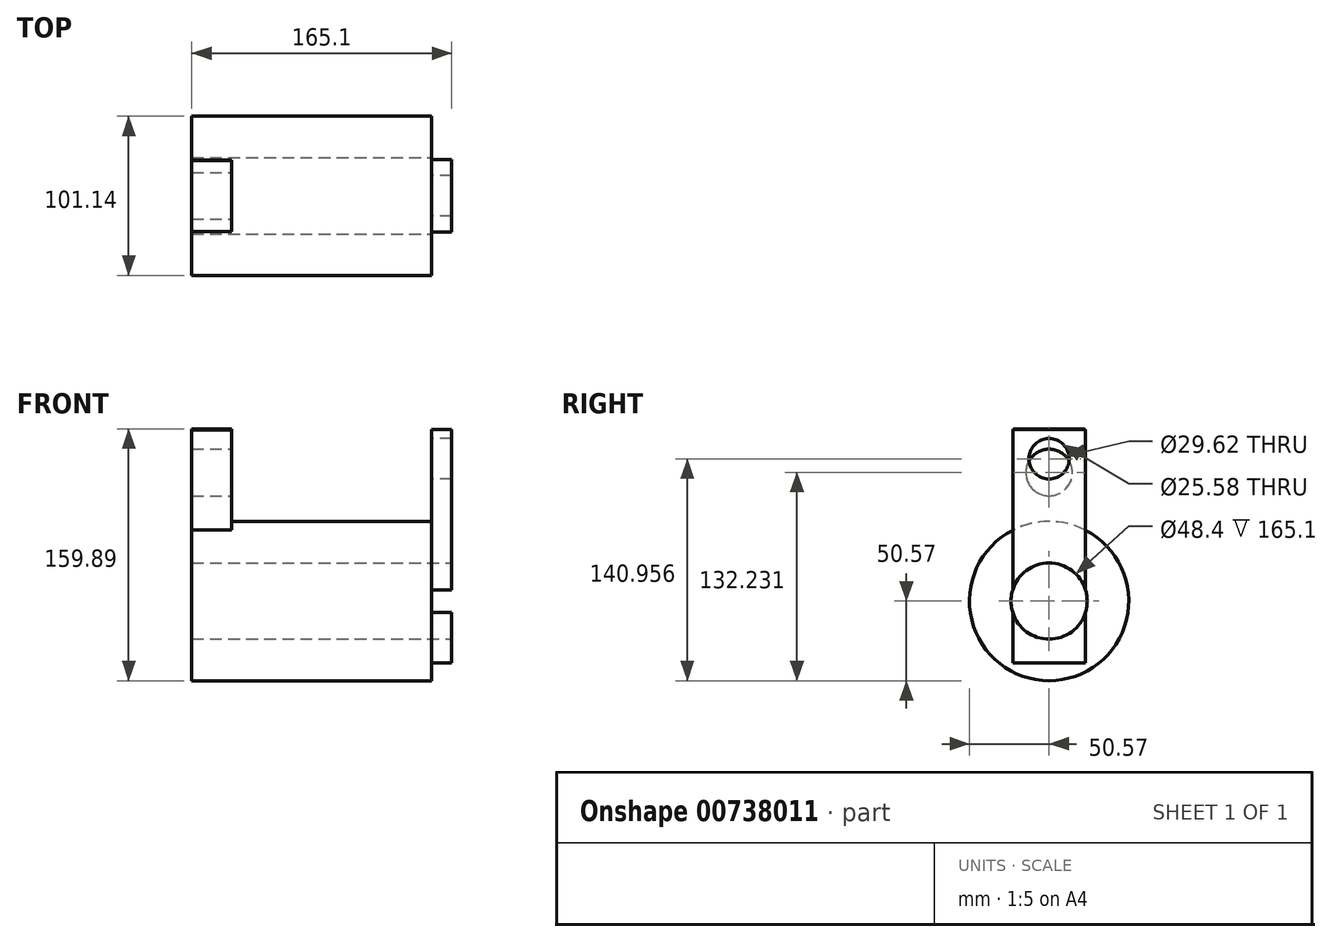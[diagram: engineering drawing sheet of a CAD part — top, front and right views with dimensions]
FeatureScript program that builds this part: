
annotation { "Feature Type Name" : "Feature", "Feature Type Description" : "" }
export const myFeature = defineFeature(function(context is Context, id is Id, definition is map)
    precondition{}
    {
        {
            var Q0;
            Q0=qCreatedBy(makeId("Right.planeOp"),FACE);
            var sketch = newSketch(context, id + "F0", { "sketchPlane" : qUnion([Q0])});
            skCircle(sketch, "E0", {"center": v(0, 0) * mm, "radius": 50.57 * mm});
            skSolve(sketch);
        }
        {
            var Q0;
            Q0 = qSketchRegion(id + "F0", true);
            extrude(context, id + "F1", {"entities" : qUnion([Q0]), "depth" : 152.4 * mm, "offsetDistance" : 25.4 * mm});
        }
        {
            var Q0;
            Q0=qCreatedBy(makeId("Right.planeOp"),FACE);
            var sketch = newSketch(context, id + "F2", { "sketchPlane" : qUnion([Q0])});
            skLineSegment(sketch, "E1.bottom", {"start": v(22.55, 109.32) * mm, "end": v(-22.55, 109.32) * mm});
            skLineSegment(sketch, "E1.top", {"start": v(22.55, -44.03) * mm, "end": v(-22.55, -44.03) * mm});
            skLineSegment(sketch, "E1.left", {"start": v(22.55, 109.32) * mm, "end": v(22.55, -44.03) * mm});
            skLineSegment(sketch, "E1.right", {"start": v(-22.55, 109.32) * mm, "end": v(-22.55, -44.03) * mm});
            skPoint(sketch, "E1.middle", {"position": v(0, 32.65) * mm});
            skSolve(sketch);
        }
        {
            var Q0;
            Q0 = qSketchRegion(id + "F2", true);
            extrude(context, id + "F3", {"entities" : qUnion([Q0]), "operationType" : NewBodyOperationType.ADD, "depth" : 25.4 * mm, "offsetDistance" : 25.4 * mm});
        }
        {
            var Q0;
            Q0=qCreatedBy(makeId("Right.planeOp"),FACE);
            var sketch = newSketch(context, id + "F4", { "sketchPlane" : qUnion([Q0])});
            skLineSegment(sketch, "E2.bottom", {"start": v(-22.66, 108.8) * mm, "end": v(22.66, 108.8) * mm});
            skLineSegment(sketch, "E2.top", {"start": v(-22.66, -44.85) * mm, "end": v(22.66, -44.85) * mm});
            skLineSegment(sketch, "E2.left", {"start": v(-22.66, 108.8) * mm, "end": v(-22.66, -44.85) * mm});
            skLineSegment(sketch, "E2.right", {"start": v(22.66, 108.8) * mm, "end": v(22.66, -44.85) * mm});
            skPoint(sketch, "E2.middle", {"position": v(0, 31.97) * mm});
            skSolve(sketch);
        }
        {
            var Q0;
            Q0 = qSketchRegion(id + "F4", true);
            extrude(context, id + "F5", {"entities" : qUnion([Q0]), "operationType" : NewBodyOperationType.ADD, "depth" : 25.4 * mm, "offsetDistance" : 25.4 * mm});
        }
        {
            var Q0;
            Q0=makeQuery(id+"F1.opExtrude","CAP_FACE",FACE,{"disambiguationData":[OSD([sQuery(id+"F0.wireOp",EDGE,"E0")])],"isStart":false});
            var sketch = newSketch(context, id + "F6", { "sketchPlane" : qUnion([Q0])});
            skLineSegment(sketch, "E3.bottom", {"start": v(-23.12, 109.08) * mm, "end": v(23.12, 109.08) * mm});
            skLineSegment(sketch, "E3.top", {"start": v(-23.12, -39.4) * mm, "end": v(23.12, -39.4) * mm});
            skLineSegment(sketch, "E3.left", {"start": v(-23.12, 109.08) * mm, "end": v(-23.12, -39.4) * mm});
            skLineSegment(sketch, "E3.right", {"start": v(23.12, 109.08) * mm, "end": v(23.12, -39.4) * mm});
            skPoint(sketch, "E3.middle", {"position": v(0, 34.84) * mm});
            skSolve(sketch);
        }
        {
            var Q0;
            {var subQ0=sQuery(id+"F6.wireOp",EDGE,"E3.top");Q0=makeQuery(id+"F6.imprint","IMPRINT",FACE,{"disambiguationData":[TD([[makeQuery(id+"F6.imprint","IMPRINT",EDGE,{"derivedFrom":subQ0}),1.0]])]});}
            var Q1;
            {var subQ0=sQuery(id+"F6.wireOp",EDGE,"E3.bottom");Q1=makeQuery(id+"F6.imprint","IMPRINT",FACE,{"disambiguationData":[TD([[makeQuery(id+"F6.imprint","IMPRINT",EDGE,{"derivedFrom":subQ0}),-1.0]])]});}
            extrude(context, id + "F7", {"entities" : qUnion([Q0, Q1]), "operationType" : NewBodyOperationType.ADD, "depth" : 25.4 * mm, "offsetDistance" : 25.4 * mm});
        }
        {
            var Q0;
            Q0=qCreatedBy(makeId("Right.planeOp"),FACE);
            var sketch = newSketch(context, id + "F8", { "sketchPlane" : qUnion([Q0])});
            skCircle(sketch, "E4", {"center": v(0, 81.66) * mm, "radius": 14.8 * mm});
            skSolve(sketch);
        }
        {
            var Q0;
            Q0 = qSketchRegion(id + "F8", true);
            var Q1;
            Q1=makeQuery(id+"F7.opExtrude","CAP_FACE",FACE,{"disambiguationData":[OSD([sQuery(id+"F6.wireOp",EDGE,"E3.bottom"),sQuery(id+"F6.wireOp",EDGE,"E3.top"),sQuery(id+"F6.wireOp",EDGE,"E3.left"),sQuery(id+"F6.wireOp",EDGE,"E3.right")])],"isStart":false});
            extrude(context, id + "F9", {"entities" : qUnion([Q0, Q1]), "operationType" : NewBodyOperationType.REMOVE, "oppositeDirection" : true, "depth" : 25.4 * mm, "offsetDistance" : 25.4 * mm, "symmetric" : true});
        }
        {
            var Q0;
            Q0=makeQuery(id+"F9.boolean.opBoolean","COPY",FACE,{"derivedFrom":makeQuery(id+"F9.opExtrude","CAP_FACE",FACE,{"disambiguationData":[OSD([sQuery(id+"F8.wireOp",EDGE,"E4")])],"isStart":true})});
            var sketch = newSketch(context, id + "F10", { "sketchPlane" : qUnion([Q0])});
            skSolve(sketch);
        }
        {
            var Q0;
            Q0=makeQuery(id+"F10.imprint","IMPRINT",FACE,{"disambiguationData":[TD([[makeQuery(id+"F10.imprint","IMPRINT",EDGE,{"derivedFrom":makeQuery(id+"F9.boolean.opBoolean","COPY",EDGE,{"derivedFrom":makeQuery(id+"F9.opExtrude","CAP_EDGE",EDGE,{"disambiguationData":[OSD([sQuery(id+"F8.wireOp",EDGE,"E4")])],"isStart":true})})}),-1.0]])]});
            extrude(context, id + "F11", {"entities" : qUnion([Q0]), "operationType" : NewBodyOperationType.REMOVE, "oppositeDirection" : true, "depth" : 25.4 * mm, "offsetDistance" : 25.4 * mm});
        }
        {
            var Q0;
            Q0=qCreatedBy(makeId("Right.planeOp"),FACE);
            var sketch = newSketch(context, id + "F12", { "sketchPlane" : qUnion([Q0])});
            skCircle(sketch, "E5", {"center": v(-7.3, 64.52) * mm, "radius": 14.02 * mm});
            skSolve(sketch);
        }
        {
            var Q0;
            Q0 = qSketchRegion(id + "F12", true);
            extrude(context, id + "F13", {"entities" : qUnion([Q0]), "operationType" : NewBodyOperationType.REMOVE, "oppositeDirection" : true, "depth" : 25.4 * mm, "offsetDistance" : 25.4 * mm});
        }
        {
            var Q0;
            Q0=makeQuery(id+"F7.opExtrude","CAP_FACE",FACE,{"disambiguationData":[OSD([sQuery(id+"F6.wireOp",EDGE,"E3.bottom"),sQuery(id+"F6.wireOp",EDGE,"E3.top"),sQuery(id+"F6.wireOp",EDGE,"E3.left"),sQuery(id+"F6.wireOp",EDGE,"E3.right")])],"isStart":true});
            var sketch = newSketch(context, id + "F14", { "sketchPlane" : qUnion([Q0])});
            skCircle(sketch, "E6", {"center": v(0, 90.39) * mm, "radius": 12.8 * mm});
            skSolve(sketch);
        }
        {
            var Q0;
            Q0 = qSketchRegion(id + "F14", true);
            extrude(context, id + "F15", {"entities" : qUnion([Q0]), "operationType" : NewBodyOperationType.REMOVE, "oppositeDirection" : true, "depth" : 25.4 * mm, "offsetDistance" : 25.4 * mm});
        }
        {
            var Q0;
            Q0=qCreatedBy(makeId("Right.planeOp"),FACE);
            var sketch = newSketch(context, id + "F16", { "sketchPlane" : qUnion([Q0])});
            skCircle(sketch, "E7", {"center": v(0, 0) * mm, "radius": 19.69 * mm});
            skSolve(sketch);
        }
        {
            var Q0;
            Q0 = qSketchRegion(id + "F16", true);
            extrude(context, id + "F17", {"entities" : qUnion([Q0]), "operationType" : NewBodyOperationType.REMOVE, "oppositeDirection" : true, "depth" : 177.8 * mm, "offsetDistance" : 25.4 * mm});
        }
        {
            var Q0;
            Q0=qCreatedBy(makeId("Right.planeOp"),FACE);
            var sketch = newSketch(context, id + "F18", { "sketchPlane" : qUnion([Q0])});
            skCircle(sketch, "E8", {"center": v(0, 0) * mm, "radius": 24.2 * mm});
            skSolve(sketch);
        }
        {
            var Q0;
            Q0=makeQuery(id+"F18.imprint","IMPRINT",FACE,{"disambiguationData":[TD([[makeQuery(id+"F18.imprint","IMPRINT",EDGE,{"derivedFrom":sQuery(id+"F18.wireOp",EDGE,"E8")}),1.0]])]});
            extrude(context, id + "F19", {"entities" : qUnion([Q0]), "operationType" : NewBodyOperationType.REMOVE, "oppositeDirection" : true, "depth" : 203.2 * mm, "offsetDistance" : 25.4 * mm, "symmetric" : true});
        }
        {
            var Q0;
            Q0=makeQuery(id+"F19.boolean.opBoolean","COPY",FACE,{"derivedFrom":makeQuery(id+"F19.opExtrude","CAP_FACE",FACE,{"disambiguationData":[OSD([sQuery(id+"F18.wireOp",EDGE,"E8")])],"isStart":true})});
            extrude(context, id + "F20", {"entities" : qUnion([Q0]), "operationType" : NewBodyOperationType.REMOVE, "oppositeDirection" : true, "depth" : 25.4 * mm, "offsetDistance" : 25.4 * mm});
        }
        {
            var Q0;
            Q0=makeQuery(id+"F20.boolean.opBoolean","COPY",FACE,{"derivedFrom":makeQuery(id+"F20.opExtrude","CAP_FACE",FACE,{"disambiguationData":[OSD([sQuery(id+"F18.wireOp",EDGE,"E8")])],"isStart":false})});
            extrude(context, id + "F21", {"entities" : qUnion([Q0]), "operationType" : NewBodyOperationType.REMOVE, "oppositeDirection" : true, "depth" : 203.2 * mm, "offsetDistance" : 25.4 * mm});
        }
    });
